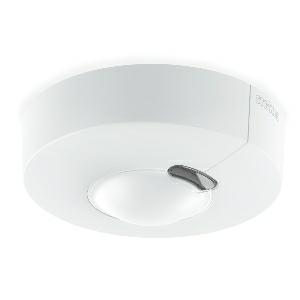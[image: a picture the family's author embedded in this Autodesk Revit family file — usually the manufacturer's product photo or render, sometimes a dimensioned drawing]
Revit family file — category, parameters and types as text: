
# Revit family: hf_3360_033736
name_source: partatom
category: Elektroinstallationen
revit_build: Autodesk Revit 2016 (Build: 20190508_0715(x64)
units: mm (PartAtom-declared; Revit-internal decimal feet)

## family parameters
Basisbauteil = Fläche
Beim Laden mit Abzugskörper schneiden = Nein
Bemaßung runder Anschluss = Durchmesser verwenden
Beschriftungsausrichtung beibehalten = Nein
Gemeinsam genutzt = Nein
Raumberechnungspunkt = Nein
Teiletyp = Normal

## types (1)
- HF 3360
    Apparent Load = 0 VA
    Beschreibung = Type: Motion detectors; Dimensions (Ø x H): 126 x 52 mm; Mains power supply: 220 – 240 V / 50 – 60 Hz; Sensor Technology: High frequency; Application, place: Indoors; Application, room: function room / ancillary room, stairwell, WC / washroom, multi-storey / underground car park, Indoors; Installation site: wall, ceiling, corner; Installation: Surface wiring; HF-system: 5,8 GHz; Electronic scalability: Yes; Mechanical scalability: No; Mounting height: 2,00 – 4,00 m; Optimum mounting height: 2,8 m; Detection: also through glass, wood and stud walls; Detection angle: 360 °; Angle of aperture: 140 °; Sneak-by guard: Yes; Reach, radial: Ø 8 m (50 m²); Reach, tangential: Ø 8 m (50 m²); Twilight setting TEACH: No; Twilight setting: 2 – 1000 lx; Time setting: 5 sec – 15 min; Control output, Dali: Broadcast 1x30 electronic ballasts; Constant-lighting control: Yes; Basic light level function: Yes; Basic light level function in per cent: 10 – 50 %; Basic light level function time: 1-30 min, all night; Basic light level function percentage, from: 10 %; Basic light level function percentage, up to: 50 %; Functions: Normal / test mode, Manual ON / ON-OFF, Constant-lighting control ON-OFF; Settings via: Remote control, Potentiometers, Smart Remote; With remote control: No; Interconnection: Yes; IP-rating: IP54; Material: Plastic; Ambient temperature: -20 – 50 °C; Colour: white; Colour, RAL: 9003; Manufacturer's Warranty: 5 years; Version: DALI-2 Application Controller - surface, rd.; PU1, EAN: 4007841033736
    Height = 0 mm  [stored 0 ft]
    Hersteller = Steinel
    Length = 126 mm
    ModVariant = Nein
    Modell = 033736
    Mounting Type = Surface mounted
    Number of Poles = 1
    OnlyDefault = Ja
    Power Factor = 1
    Product Name = HF 3360
    Product group = Sensor-switched indoor light
    ProductGroupID = 30
    Protection Class = Protection class
    Protection Degree = IP 54
    RlxData = <blob elided: 37737 chars, md5=36e87d3a>
    SensorDataFile = {"IESDataFiles":[]}
    Typenbild = produkt1_033736.jpg
    Typenkommentare = Product without accessories
    URL = http://relux.com
    VarID = ---
    Voltage = 0 V
    Vorgabe-Ansicht = 1800 mm
    Weight = 0.00 kg
    Width = 0 mm  [stored 0 ft]

note: [stored X ft] marks values corroborated as IEEE doubles in the binary element streams (Revit-internal decimal feet)

## geometry (parser evidence)
native form markers: Sweep x7
no freeform markers — native parametric forms only
